# Revit family: sink-undercounter-Kohler-Caxton-2209
name_source: partatom
category: Plumbing Fixtures
revit_build: Autodesk Revit Architecture 2013 (Build: 20130531_2115(x64)
units: mm (PartAtom-declared; Revit-internal decimal feet)

## types (13) — shared parameters
Assembly Code = D2010400
CW Connection = No
Description = Caxton® undercounter lavatory
HW Connection = No
Height = 0' - 7 1/2"
Length = 1' - 2"
Manufacturer = Kohler
Model = K-2209
Product Documentation Link = http://www.us.kohler.com
Product Page URL = http://www.us.kohler.com
Sanitary Connector = Sanitary Connection
Sanitary Diameter = 1"
Sanitary Radius = 1"
URL = http://www.us.kohler.com
Waste Connection = Yes
Width = 1' - 5"
zero-valued in all types: CWFU, HWFU, WFU

## per-type parameters (varying)
| type | Default Elevation | Finish | Vent Connection |
| Vitreous_China-0-White | 7' - 0" | Vitreous China-Kohler-0-White | Yes |
| Vitreous_China-6-Skylight | 0' - 0" | Vitreous China-Kohler-6-Skylight | No |
| Vitreous_China-7-Black_Black | 0' - 0" | Vitreous China-Kohler-7-Black Black | No |
| Vitreous_China-33-Mexican_Sand | 0' - 0" | Vitreous China-Kohler-33-Mexican Sand | No |
| Vitreous_China-47-Almond | 0' - 0" | Vitreous China-Kohler-47-Almond | No |
| Vitreous_China-55-Innocent_Blush | 0' - 0" | Vitreous China-Kohler-55-Innocent Blush | No |
| Vitreous_China-58-Thunder_Grey | 0' - 0" | Vitreous China-Kohler-58-Thunder Grey | No |
| Vitreous_China-95-Ice_Grey | 0' - 0" | Vitreous China-Kohler-95-Ice Grey | No |
| Vitreous_China-96-Biscuit | 0' - 0" | Vitreous China-Kohler-96-Biscuit | No |
| Vitreous_China-G9-Sandbar | 0' - 0" | Vitreous China-Kohler-G9-Sandbar | No |
| Vitreous_China-K4-Cashmere | 0' - 0" | Vitreous China-Kohler-K4-Cashmere | No |
| Vitreous_China-NG-Tea_Green | 2' - 7" | Vitreous China-Kohler-NG-Tea Green | No |
| Vitreous_China-Y2-Sunlight | 0' - 0" | Vitreous China-Kohler-Y2-Sunlight | No |

## geometry (parser evidence)
native form markers: Blend x44, Sweep x2
no freeform markers — native parametric forms only
